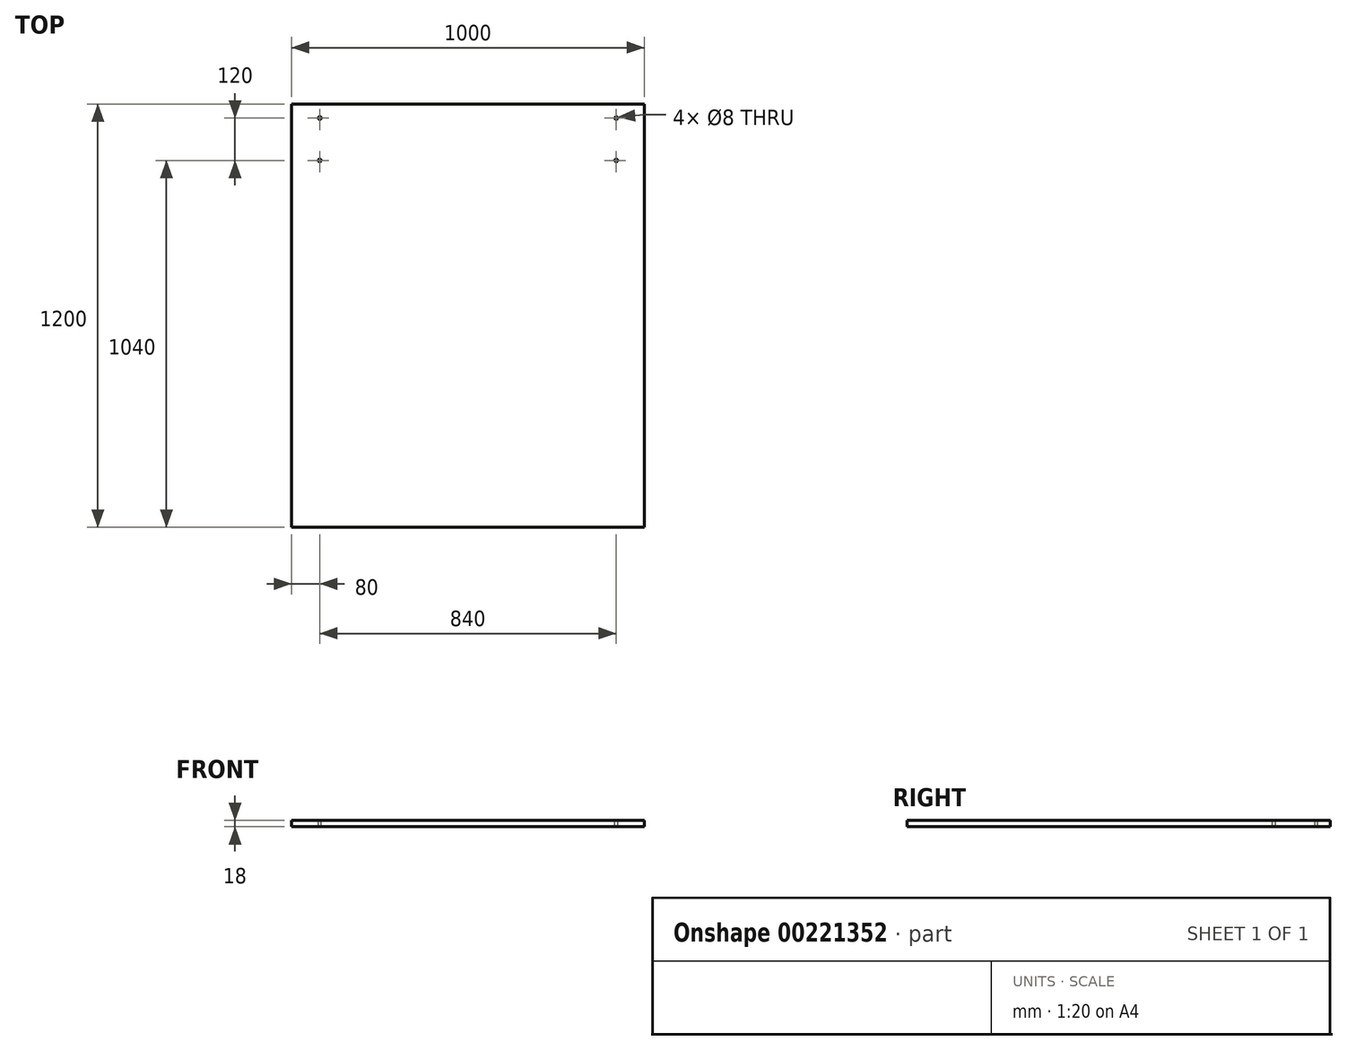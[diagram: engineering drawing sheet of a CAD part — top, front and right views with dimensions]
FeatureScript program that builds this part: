
annotation { "Feature Type Name" : "Feature", "Feature Type Description" : "" }
export const myFeature = defineFeature(function(context is Context, id is Id, definition is map)
    precondition{}
    {
        {
            var Q0;
            Q0=qCreatedBy(makeId("Top.planeOp"),FACE);
            var sketch = newSketch(context, id + "F0", { "sketchPlane" : qUnion([Q0])});
            skLineSegment(sketch, "E0.bottom", {"start": v(500, -600) * mm, "end": v(-500, -600) * mm});
            skLineSegment(sketch, "E0.top", {"start": v(500, 600) * mm, "end": v(-500, 600) * mm});
            skLineSegment(sketch, "E0.left", {"start": v(500, -600) * mm, "end": v(500, 600) * mm});
            skLineSegment(sketch, "E0.right", {"start": v(-500, -600) * mm, "end": v(-500, 600) * mm});
            skPoint(sketch, "E0.middle", {"position": v(0, 0) * mm});
            skSolve(sketch);
        }
        {
            var Q0;
            Q0 = qSketchRegion(id + "F0", true);
            extrude(context, id + "F1", {"entities" : qUnion([Q0]), "depth" : 18 * mm});
        }
        {
            var Q0;
            Q0=makeQuery(id+"F1.opExtrude","CAP_FACE",FACE,{"disambiguationData":[OSD([sQuery(id+"F0.wireOp",EDGE,"E0.bottom"),sQuery(id+"F0.wireOp",EDGE,"E0.top"),sQuery(id+"F0.wireOp",EDGE,"E0.left"),sQuery(id+"F0.wireOp",EDGE,"E0.right")])],"isStart":false});
            var sketch = newSketch(context, id + "F2", { "sketchPlane" : qUnion([Q0])});
            skCircle(sketch, "E1", {"center": v(-420, 560) * mm, "radius": 4 * mm});
            skCircle(sketch, "E2", {"center": v(420, 560) * mm, "radius": 4 * mm});
            skCircle(sketch, "E3", {"center": v(-420, 440) * mm, "radius": 4 * mm});
            skCircle(sketch, "E4", {"center": v(420, 440) * mm, "radius": 4 * mm});
            skSolve(sketch);
        }
        {
            var Q0;
            Q0 = qSketchRegion(id + "F2", true);
            extrude(context, id + "F3", {"entities" : qUnion([Q0]), "operationType" : NewBodyOperationType.REMOVE, "oppositeDirection" : true, "depth" : 25 * mm});
        }
    });
